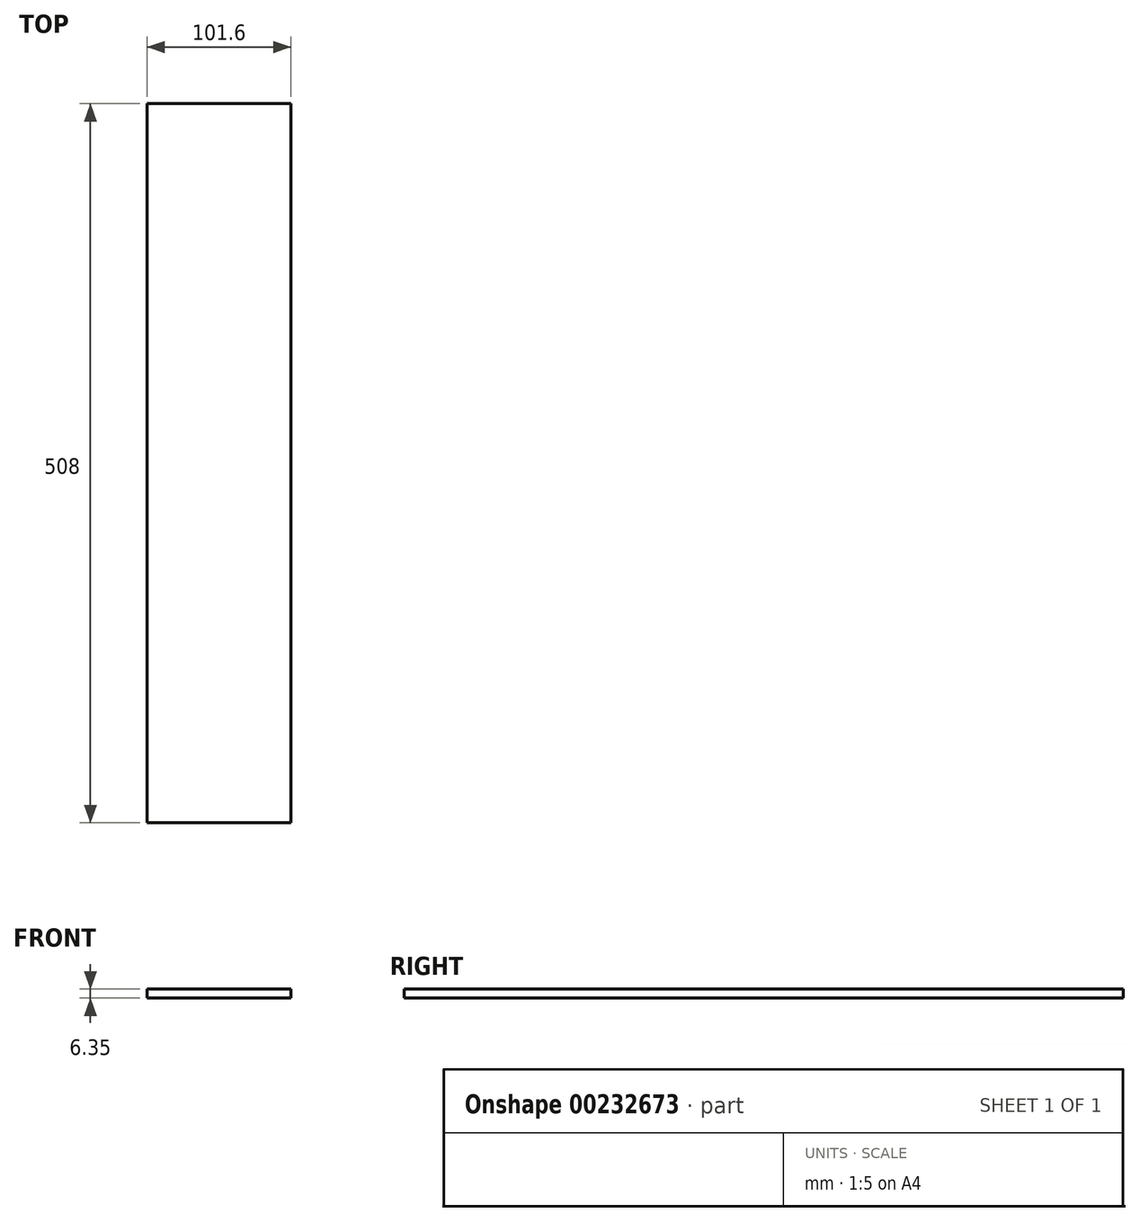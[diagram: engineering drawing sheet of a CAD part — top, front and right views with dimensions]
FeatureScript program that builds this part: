
annotation { "Feature Type Name" : "Feature", "Feature Type Description" : "" }
export const myFeature = defineFeature(function(context is Context, id is Id, definition is map)
    precondition{}
    {
        {
            var Q0;
            Q0=qCreatedBy(makeId("Top.planeOp"),FACE);
            var sketch = newSketch(context, id + "F0", { "sketchPlane" : qUnion([Q0])});
            skLineSegment(sketch, "E0.bottom", {"start": v(-50.8, 254) * mm, "end": v(50.8, 254) * mm});
            skLineSegment(sketch, "E0.top", {"start": v(-50.8, -254) * mm, "end": v(50.8, -254) * mm});
            skLineSegment(sketch, "E0.left", {"start": v(-50.8, 254) * mm, "end": v(-50.8, -254) * mm});
            skLineSegment(sketch, "E0.right", {"start": v(50.8, 254) * mm, "end": v(50.8, -254) * mm});
            skPoint(sketch, "E0.middle", {"position": v(0, 0) * mm});
            skSolve(sketch);
        }
        {
            var Q0;
            Q0=makeQuery(id+"F0.imprint","IMPRINT",FACE,{"disambiguationData":[TD([[makeQuery(id+"F0.imprint","IMPRINT",EDGE,{"derivedFrom":sQuery(id+"F0.wireOp",EDGE,"E0.bottom")}),-1.0]])]});
            extrude(context, id + "F1", {"entities" : qUnion([Q0]), "depth" : 6.35 * mm});
        }
    });
